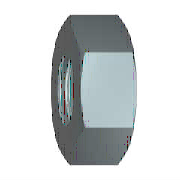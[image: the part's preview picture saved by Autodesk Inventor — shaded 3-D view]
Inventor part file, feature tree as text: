
AUTODESK INVENTOR PART (.ipt)
format: ipt  version: 2022 (Build 260153000, 153)  size: 165,888 bytes
history: native  units: mm (DEFAULTED — no unit token found)
features: sketch x3, other x2, extrude x1, hole x1, plane x1
ambient origin geometry x7: Origin, YZ Plane, XZ Plane, X Axis, Y Axis, Z Axis, Center Point
bodies: Solid1 (feature_tree)
feature tree (8):
  extrude  "Базовый элемент"  Depth=6.928203mm
  other  "Фаска1"
  hole  "Резьба"  [1 undecoded]
  other  "Work Axis1"
  plane  "Work Plane1"
  sketch  "Эскиз1"
  sketch  "Эскиз2"
  sketch  "Эскиз3"
note: 1 required parameter value undecoded (feature->parameter linkage not recoverable at this tier; creation-order binding heuristic only, values carry confidence <= 0.55)
